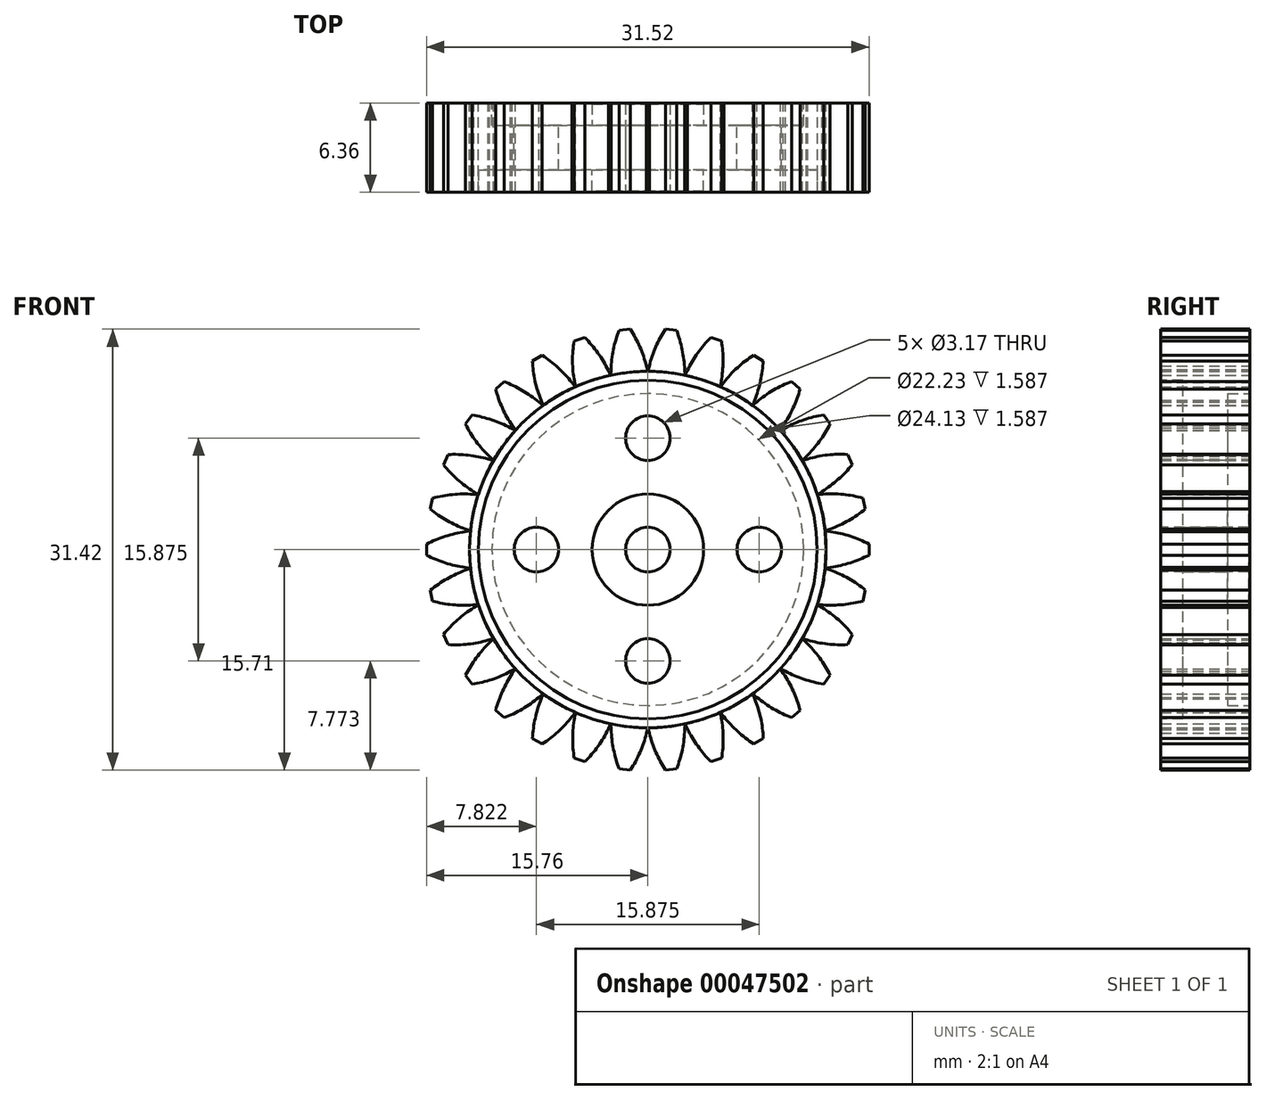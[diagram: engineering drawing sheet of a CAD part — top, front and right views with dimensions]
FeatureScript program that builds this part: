
annotation { "Feature Type Name" : "Feature", "Feature Type Description" : "" }
export const myFeature = defineFeature(function(context is Context, id is Id, definition is map)
    precondition{}
    {
        {
            var Q0;
            Q0=qCreatedBy(makeId("Front.planeOp"),FACE);
            var sketch = newSketch(context, id + "F0", { "sketchPlane" : qUnion([Q0])});
            skCircle(sketch, "E0", {"center": v(0, 0) * mm, "radius": 12.7 * mm});
            skSolve(sketch);
        }
        {
            var Q0;
            Q0 = qSketchRegion(id + "F0", true);
            extrude(context, id + "F1", {"entities" : qUnion([Q0]), "endBound" : BoundingType.SYMMETRIC, "depth" : 6.35 * mm});
        }
        {
            var Q0;
            Q0=makeQuery(id+"F1.opExtrude","CAP_FACE",FACE,{"disambiguationData":[OSD([sQuery(id+"F0.wireOp",EDGE,"E0")])],"isStart":true});
            var sketch = newSketch(context, id + "F2", { "sketchPlane" : qUnion([Q0])});
            skLineSegment(sketch, "E1", {"start": v(15.76, 0) * mm, "end": v(15.76, 0.4) * mm});
            skLineSegment(sketch, "E2", {"start": v(15.76, 0) * mm, "end": v(15.76, -0.4) * mm});
            skLineSegment(sketch, "E3", {"start": v(13.02, -1.27) * mm, "end": v(12.63, -1.33) * mm});
            skLineSegment(sketch, "E4", {"start": v(13.02, 1.27) * mm, "end": v(12.63, 1.33) * mm});
            skArc(sketch, "E5", {"start": v(12.63, -1.33) * mm, "mid": v(12.7, 0) * mm, "end": v(12.63, 1.33) * mm});
            skLineSegment(sketch, "E6", {"start": v(12.63, 1.33) * mm, "end": v(12.63, -1.33) * mm, "construction": true});
            skArc(sketch, "E7", {"start": v(15.76, 0.4) * mm, "mid": v(14.42, 0.94) * mm, "end": v(13.02, 1.27) * mm});
            skArc(sketch, "E8", {"start": v(13.02, -1.27) * mm, "mid": v(14.43, -0.95) * mm, "end": v(15.76, -0.4) * mm});
            skPoint(sketch, "E9.orphan", {"position": v(15.76, 0.8) * mm});
            skPoint(sketch, "E10.orphan", {"position": v(15.76, -0.8) * mm});
            skSolve(sketch);
        }
        {
            var Q0;
            Q0=makeQuery(id+"F2.imprint","IMPRINT",FACE,{"disambiguationData":[TD([[makeQuery(id+"F2.imprint","IMPRINT",EDGE,{"derivedFrom":sQuery(id+"F2.wireOp",EDGE,"E1")}),1.0]])]});
            extrude(context, id + "F3", {"entities" : qUnion([Q0]), "oppositeDirection" : true, "depth" : 6.35 * mm});
        }
        {
            var Q0;
            Q0=makeQuery(id+"F3.opExtrude","SWEPT_BODY",BODY,{"disambiguationData":[OSD([sQuery(id+"F2.wireOp",EDGE,"E1"),sQuery(id+"F2.wireOp",EDGE,"E2"),sQuery(id+"F2.wireOp",EDGE,"E3"),sQuery(id+"F2.wireOp",EDGE,"E4"),sQuery(id+"F2.wireOp",EDGE,"E5")])]});
            var Q1;
            Q1=makeQuery(id+"F1.opExtrude","CAP_EDGE",EDGE,{"disambiguationData":[OSD([sQuery(id+"F0.wireOp",EDGE,"E0")])],"isStart":true});
            circularPattern(context, id + "F4", {"entities" : qUnion([Q0]), "axis" : qUnion([Q1]), "angle" : 360 * degree, "instanceCount" : 30, "equalSpace" : true});
        }
        {
            var Q0;
            Q0=makeQuery(id+"F1.opExtrude","CAP_FACE",FACE,{"disambiguationData":[OSD([sQuery(id+"F0.wireOp",EDGE,"E0")])],"isStart":true});
            var sketch = newSketch(context, id + "F5", { "sketchPlane" : qUnion([Q0])});
            skCircle(sketch, "E11", {"center": v(0, 0) * mm, "radius": 11.11 * mm});
            skSolve(sketch);
        }
        {
            var Q0;
            Q0=makeQuery(id+"F5.imprint","IMPRINT",FACE,{"disambiguationData":[TD([[makeQuery(id+"F5.imprint","IMPRINT",EDGE,{"derivedFrom":sQuery(id+"F5.wireOp",EDGE,"E11")}),1.0]])]});
            extrude(context, id + "F6", {"entities" : qUnion([Q0]), "operationType" : NewBodyOperationType.REMOVE, "oppositeDirection" : true, "depth" : 1.59 * mm});
        }
        {
            var Q0;
            Q0=makeQuery(id+"F1.opExtrude","CAP_FACE",FACE,{"disambiguationData":[OSD([sQuery(id+"F0.wireOp",EDGE,"E0")])],"isStart":false});
            var sketch = newSketch(context, id + "F7", { "sketchPlane" : qUnion([Q0])});
            skCircle(sketch, "E12", {"center": v(0, 0) * mm, "radius": 12.07 * mm});
            skSolve(sketch);
        }
        {
            var Q0;
            Q0=makeQuery(id+"F7.imprint","IMPRINT",FACE,{"disambiguationData":[TD([[makeQuery(id+"F7.imprint","IMPRINT",EDGE,{"derivedFrom":sQuery(id+"F7.wireOp",EDGE,"E12")}),1.0]])]});
            extrude(context, id + "F8", {"entities" : qUnion([Q0]), "operationType" : NewBodyOperationType.REMOVE, "oppositeDirection" : true, "depth" : 1.59 * mm});
        }
        {
            var Q0;
            Q0=makeQuery(id+"F8.boolean.opBoolean","COPY",FACE,{"derivedFrom":makeQuery(id+"F8.opExtrude","CAP_FACE",FACE,{"disambiguationData":[OSD([sQuery(id+"F7.wireOp",EDGE,"E12")])],"isStart":false})});
            var sketch = newSketch(context, id + "F9", { "sketchPlane" : qUnion([Q0])});
            skCircle(sketch, "E13", {"center": v(0, 7.94) * mm, "radius": 1.59 * mm});
            skSolve(sketch);
        }
        {
            var Q0;
            Q0=makeQuery(id+"F9.imprint","IMPRINT",FACE,{"disambiguationData":[TD([[makeQuery(id+"F9.imprint","IMPRINT",EDGE,{"derivedFrom":sQuery(id+"F9.wireOp",EDGE,"E13")}),1.0]])]});
            extrude(context, id + "F10", {"entities" : qUnion([Q0]), "operationType" : NewBodyOperationType.REMOVE, "oppositeDirection" : true, "depth" : 3.3 * mm});
        }
        {
            var Q0;
            Q0=makeQuery(id+"F6.boolean.opBoolean","COPY",FACE,{"derivedFrom":makeQuery(id+"F6.opExtrude","CAP_FACE",FACE,{"disambiguationData":[OSD([sQuery(id+"F5.wireOp",EDGE,"E11")])],"isStart":false})});
            var sketch = newSketch(context, id + "F11", { "sketchPlane" : qUnion([Q0])});
            skCircle(sketch, "E14", {"center": v(-7.94, 0) * mm, "radius": 1.59 * mm});
            skSolve(sketch);
        }
        {
            var Q0;
            Q0=makeQuery(id+"F11.imprint","IMPRINT",FACE,{"disambiguationData":[TD([[makeQuery(id+"F11.imprint","IMPRINT",EDGE,{"derivedFrom":sQuery(id+"F11.wireOp",EDGE,"E14")}),-1.0]])]});
            var sketch = newSketch(context, id + "F12", { "sketchPlane" : qUnion([Q0])});
            skCircle(sketch, "E15", {"center": v(0, -7.94) * mm, "radius": 1.59 * mm});
            skSolve(sketch);
        }
        {
            var Q0;
            Q0=makeQuery(id+"F11.imprint","IMPRINT",FACE,{"disambiguationData":[TD([[makeQuery(id+"F11.imprint","IMPRINT",EDGE,{"derivedFrom":sQuery(id+"F11.wireOp",EDGE,"E14")}),-1.0]])]});
            var sketch = newSketch(context, id + "F13", { "sketchPlane" : qUnion([Q0])});
            skCircle(sketch, "E16", {"center": v(7.94, 0) * mm, "radius": 1.59 * mm});
            skSolve(sketch);
        }
        {
            var Q0;
            Q0=makeQuery(id+"F11.imprint","IMPRINT",FACE,{"disambiguationData":[TD([[makeQuery(id+"F11.imprint","IMPRINT",EDGE,{"derivedFrom":sQuery(id+"F11.wireOp",EDGE,"E14")}),1.0]])]});
            extrude(context, id + "F14", {"entities" : qUnion([Q0]), "operationType" : NewBodyOperationType.REMOVE, "oppositeDirection" : true, "depth" : 3.3 * mm});
        }
        {
            var Q0;
            Q0=makeQuery(id+"F12.imprint","IMPRINT",FACE,{"disambiguationData":[TD([[makeQuery(id+"F12.imprint","IMPRINT",EDGE,{"derivedFrom":sQuery(id+"F12.wireOp",EDGE,"E15")}),1.0]])]});
            extrude(context, id + "F15", {"entities" : qUnion([Q0]), "operationType" : NewBodyOperationType.REMOVE, "oppositeDirection" : true, "depth" : 3.3 * mm});
        }
        {
            var Q0;
            Q0=makeQuery(id+"F13.imprint","IMPRINT",FACE,{"disambiguationData":[TD([[makeQuery(id+"F13.imprint","IMPRINT",EDGE,{"derivedFrom":sQuery(id+"F13.wireOp",EDGE,"E16")}),1.0]])]});
            extrude(context, id + "F16", {"entities" : qUnion([Q0]), "operationType" : NewBodyOperationType.REMOVE, "oppositeDirection" : true, "depth" : 3.3 * mm});
        }
        {
            var Q0;
            Q0=makeQuery(id+"F8.boolean.opBoolean","COPY",FACE,{"derivedFrom":makeQuery(id+"F8.opExtrude","CAP_FACE",FACE,{"disambiguationData":[OSD([sQuery(id+"F7.wireOp",EDGE,"E12")])],"isStart":false})});
            var sketch = newSketch(context, id + "F17", { "sketchPlane" : qUnion([Q0])});
            skCircle(sketch, "E17", {"center": v(0, 0) * mm, "radius": 3.97 * mm});
            skSolve(sketch);
        }
        {
            var Q0;
            Q0=makeQuery(id+"F17.imprint","IMPRINT",FACE,{"disambiguationData":[TD([[makeQuery(id+"F17.imprint","IMPRINT",EDGE,{"derivedFrom":sQuery(id+"F17.wireOp",EDGE,"E17")}),1.0]])]});
            extrude(context, id + "F18", {"entities" : qUnion([Q0]), "depth" : 1.52 * mm});
        }
        {
            var Q0;
            Q0=makeQuery(id+"F18.opExtrude","SWEPT_BODY",BODY,{"disambiguationData":[OSD([sQuery(id+"F17.wireOp",EDGE,"E17")])]});
            var Q1;
            Q1=qCreatedBy(makeId("Front.planeOp"),FACE);
            mirror(context, id + "F19", {"operationType" : NewBodyOperationType.ADD, "entities" : qUnion([Q0]), "mirrorPlane" : qUnion([Q1])});
        }
        {
            var Q0;
            Q0=makeQuery(id+"F18.opExtrude","CAP_FACE",FACE,{"disambiguationData":[OSD([sQuery(id+"F17.wireOp",EDGE,"E17")])],"isStart":false});
            var sketch = newSketch(context, id + "F20", { "sketchPlane" : qUnion([Q0])});
            skCircle(sketch, "E18", {"center": v(0, 0) * mm, "radius": 1.59 * mm});
            skSolve(sketch);
        }
        {
            var Q0;
            Q0=makeQuery(id+"F20.imprint","IMPRINT",FACE,{"disambiguationData":[TD([[makeQuery(id+"F20.imprint","IMPRINT",EDGE,{"derivedFrom":sQuery(id+"F20.wireOp",EDGE,"E18")}),1.0]])]});
            extrude(context, id + "F21", {"entities" : qUnion([Q0]), "operationType" : NewBodyOperationType.REMOVE, "oppositeDirection" : true, "depth" : 25.4 * mm});
        }
    });
